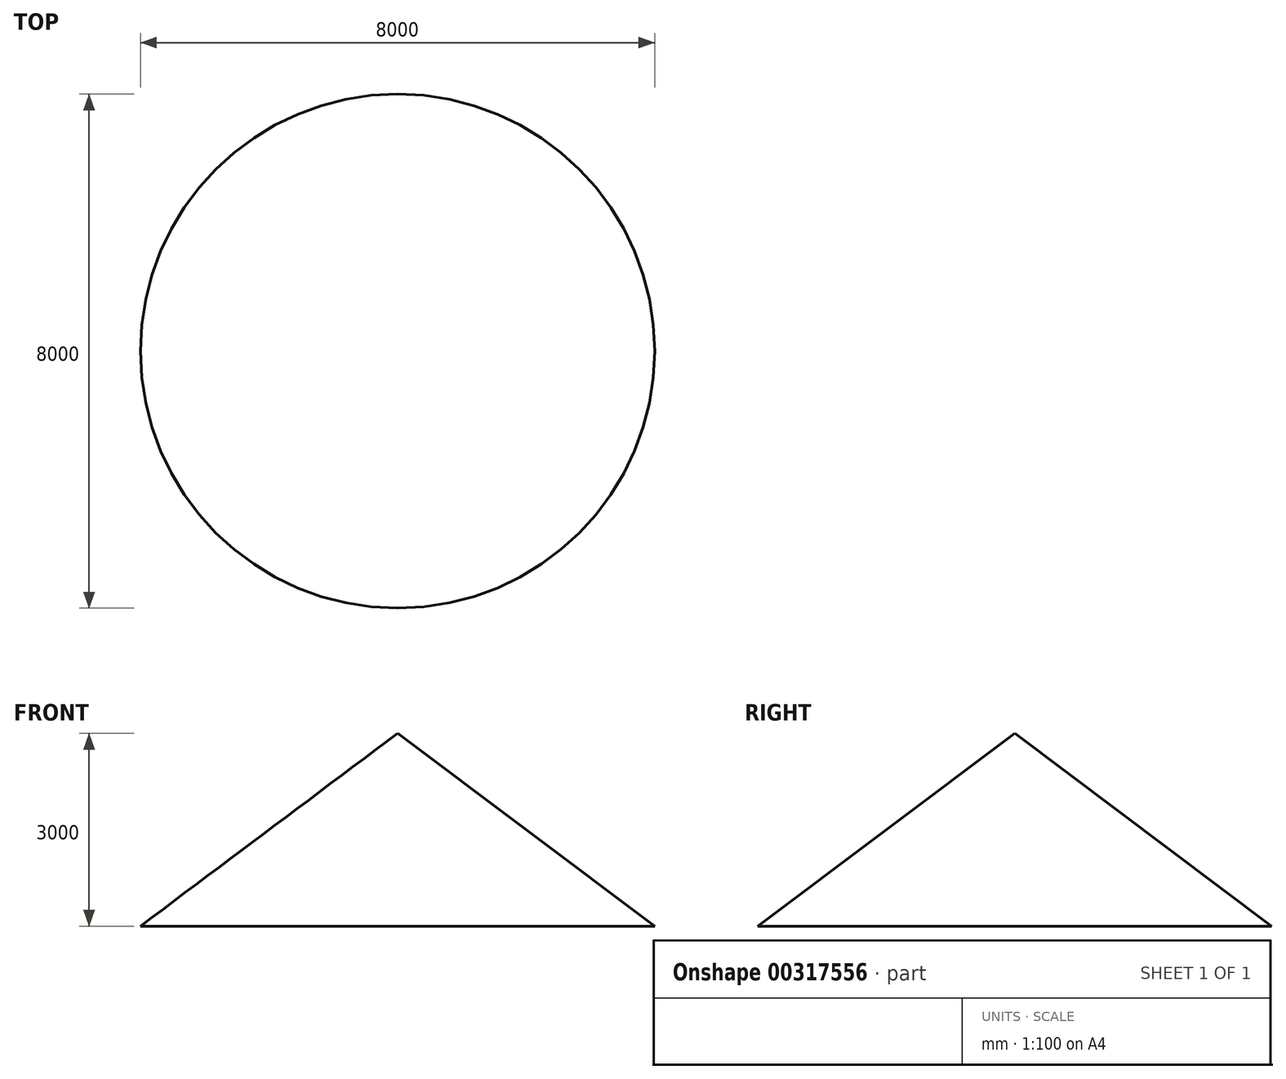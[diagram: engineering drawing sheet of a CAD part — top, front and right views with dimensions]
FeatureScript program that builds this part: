
annotation { "Feature Type Name" : "Feature", "Feature Type Description" : "" }
export const myFeature = defineFeature(function(context is Context, id is Id, definition is map)
    precondition{}
    {
        {
            var Q0;
            Q0=qCreatedBy(makeId("Front.planeOp"),FACE);
            var sketch = newSketch(context, id + "F0", { "sketchPlane" : qUnion([Q0])});
            skLineSegment(sketch, "E0", {"start": v(0, 0) * mm, "end": v(4000, 0) * mm});
            skLineSegment(sketch, "E1", {"start": v(0, 0) * mm, "end": v(0, 3000) * mm});
            skLineSegment(sketch, "E2", {"start": v(0, 3000) * mm, "end": v(4000, 0) * mm});
            skSolve(sketch);
        }
        {
            var Q0;
            Q0 = qSketchRegion(id + "F0", true);
            var Q1;
            Q1=sQuery(id+"F0.wireOp",EDGE,"E1");
            revolve(context, id + "F1", {"entities" : qUnion([Q0]), "axis" : qUnion([Q1]), "revolveType" : RevolveType.FULL});
        }
    });
